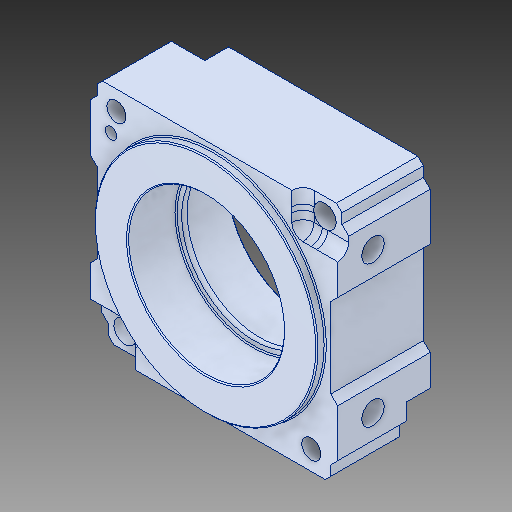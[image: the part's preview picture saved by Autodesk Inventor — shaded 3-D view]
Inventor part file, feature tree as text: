
AUTODESK INVENTOR PART (.ipt)
format: ipt  version: 2017 (Build 210142000, 142)  size: 266,752 bytes
history: native  units: in
note: dims shown in document units (in); Inventor stores cm internally (conversion verified against a paired STEP export)
features: chamfer x1
ambient origin geometry x8: Origin, YZ Plane, XZ Plane, XY Plane, X Axis, Y Axis, Z Axis, Center Point
bodies: Solid1 (feature_tree)
feature tree (1):
  chamfer  "Chamfer2"  [1 undecoded]
note: 1 required parameter value undecoded (feature->parameter linkage not recoverable at this tier; creation-order binding heuristic only, values carry confidence <= 0.55)
